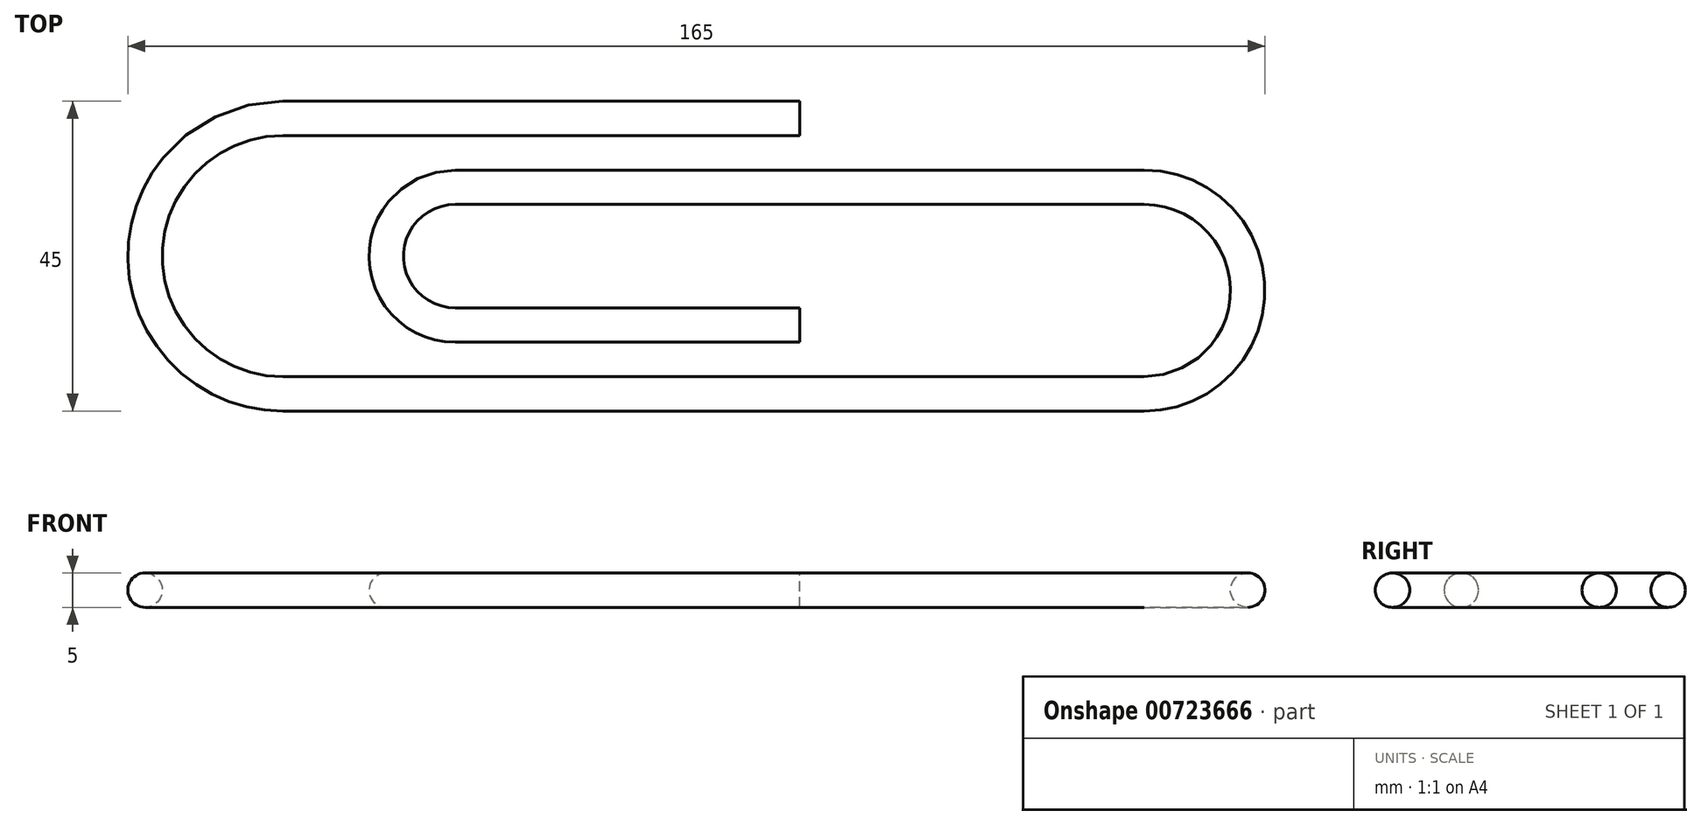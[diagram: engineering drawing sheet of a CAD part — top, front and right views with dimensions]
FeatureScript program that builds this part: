
annotation { "Feature Type Name" : "Feature", "Feature Type Description" : "" }
export const myFeature = defineFeature(function(context is Context, id is Id, definition is map)
    precondition{}
    {
        {
            var Q0;
            Q0=qCreatedBy(makeId("Top.planeOp"), FACE);
            var sketch = newSketch(context, id + "F0", { "sketchPlane" : qUnion([Q0])});
            skLineSegment(sketch, "E0", {"start": v(0, 0) * mm, "end": v(-75, 0) * mm});
            skArc(sketch, "E1", {"start": v(-75, 0) * mm, "mid": v(-95, -20) * mm, "end": v(-75, -40) * mm});
            skLineSegment(sketch, "E2", {"start": v(-75, -40) * mm, "end": v(50, -40) * mm});
            skArc(sketch, "E3", {"start": v(50, -40) * mm, "mid": v(65, -25) * mm, "end": v(50, -10) * mm});
            skLineSegment(sketch, "E4", {"start": v(50, -10) * mm, "end": v(-50, -10) * mm});
            skArc(sketch, "E5", {"start": v(-50, -10) * mm, "mid": v(-60, -20) * mm, "end": v(-50, -30) * mm});
            skLineSegment(sketch, "E6", {"start": v(-50, -30) * mm, "end": v(0, -30) * mm});
            skSolve(sketch);
        }
        {
            var Q0;
            Q0=qCreatedBy(makeId("Right.planeOp"), FACE);
            var sketch = newSketch(context, id + "F1", { "sketchPlane" : qUnion([Q0])});
            skCircle(sketch, "E7", {"center": v(0, 0) * mm, "radius": 2.5 * mm});
            skSolve(sketch);
        }
        {
            var Q0;
            Q0 = qSketchRegion(id + "F1", true);
            var Q1;
            Q1 = qConstructionFilter(qBodyType(qCreatedBy(id + "F0" ,EDGE), BodyType.WIRE), ConstructionObject.NO);
            sweep(context, id + "F2", {"profiles" : qUnion([Q0]), "path" : qUnion([Q1])});
        }
    });
